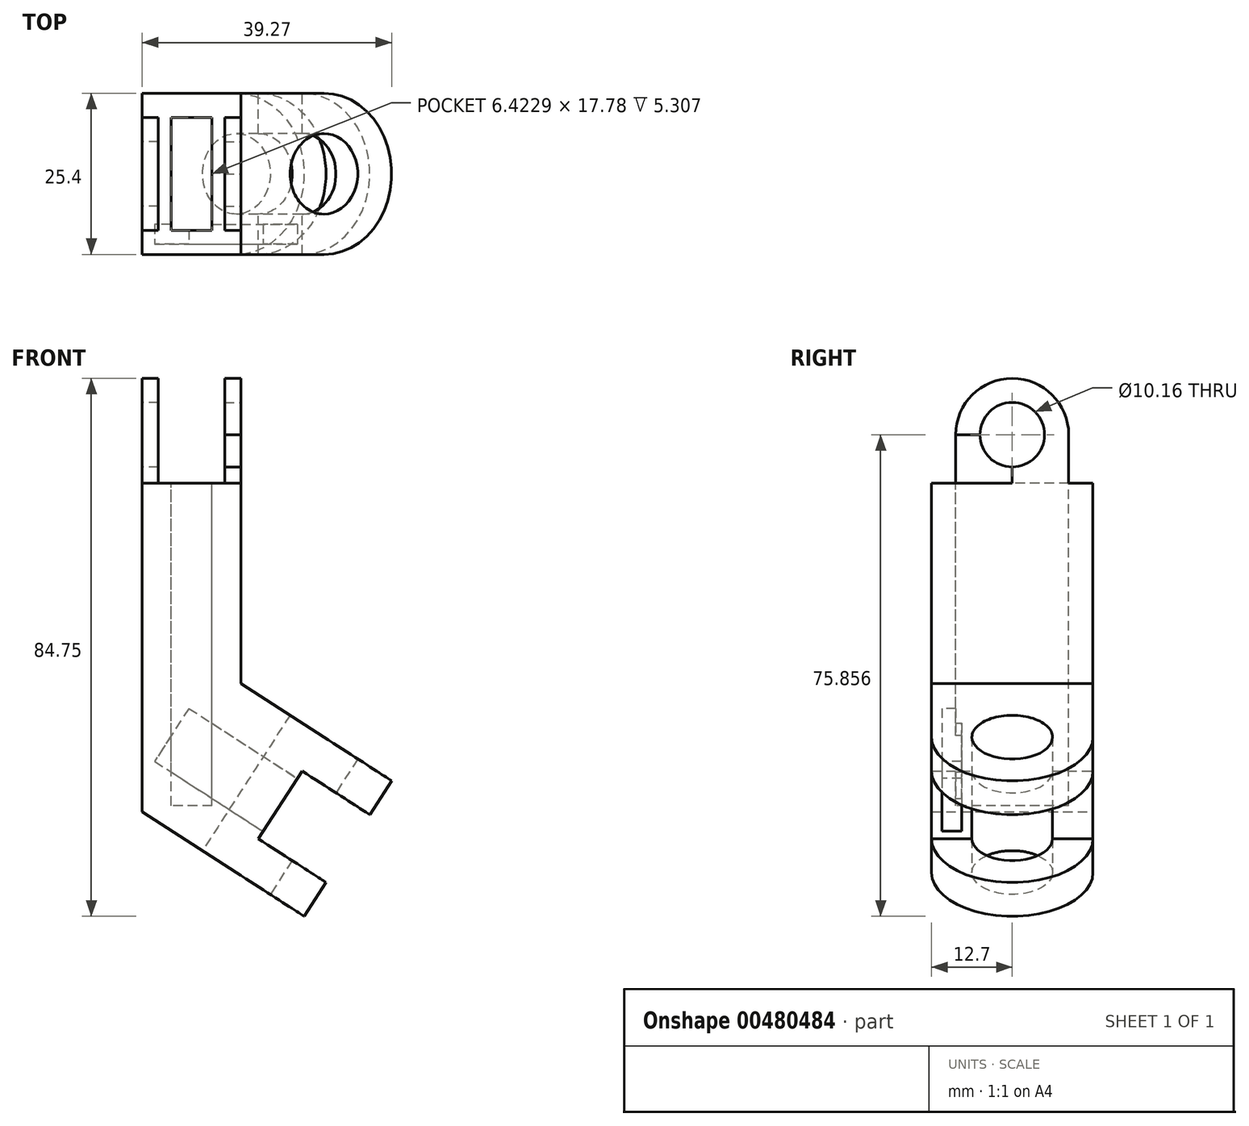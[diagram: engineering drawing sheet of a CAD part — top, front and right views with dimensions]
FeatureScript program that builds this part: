
annotation { "Feature Type Name" : "Feature", "Feature Type Description" : "" }
export const myFeature = defineFeature(function(context is Context, id is Id, definition is map)
    precondition{}
    {
        {
            var Q0;
            Q0=qCreatedBy(makeId("Front.planeOp"),FACE);
            var sketch = newSketch(context, id + "F0", { "sketchPlane" : qUnion([Q0])});
            skLineSegment(sketch, "E0", {"start": v(9.9, -37.3) * mm, "end": v(-3.19, -28.84) * mm});
            skLineSegment(sketch, "E1", {"start": v(-3.9, -58.63) * mm, "end": v(-18.71, -49.05) * mm});
            skLineSegment(sketch, "E2", {"start": v(-18.71, -49.05) * mm, "end": v(-18.71, 2.72) * mm});
            skLineSegment(sketch, "E3", {"start": v(-18.71, 2.72) * mm, "end": v(-3.19, 2.72) * mm});
            skLineSegment(sketch, "E4", {"start": v(-3.06, -57.34) * mm, "end": v(9.35, -38.14) * mm});
            skPoint(sketch, "E5.start.orphan", {"position": v(9.92, -52.43) * mm});
            skLineSegment(sketch, "E6", {"start": v(-3.06, -57.34) * mm, "end": v(-3.9, -58.63) * mm});
            skLineSegment(sketch, "E7", {"start": v(-3.9, -58.63) * mm, "end": v(9.9, -37.3) * mm});
            skPoint(sketch, "E8.orphan", {"position": v(3.03, -63.1) * mm});
            skPoint(sketch, "E9.start.orphan", {"position": v(5.9, -63.13) * mm});
            skPoint(sketch, "E10.start.orphan", {"position": v(18.01, -44.36) * mm});
            skPoint(sketch, "E11.orphan", {"position": v(16.81, -41.76) * mm});
            skLineSegment(sketch, "E12", {"start": v(-3.19, 2.72) * mm, "end": v(-3.19, -28.84) * mm});
            skPoint(sketch, "E13.orphan", {"position": v(-4.93, -27.71) * mm});
            skSolve(sketch);
        }
        {
            var Q0;
            {var subQ1=sQuery(id+"F0.wireOp",EDGE,"E0");Q0=makeQuery(id+"F0.imprint","IMPRINT",FACE,{"disambiguationData":[TD([[makeQuery(id+"F0.imprint","IMPRINT",EDGE,{"derivedFrom":subQ1}),1.0]])]});}
            extrude(context, id + "F1", {"entities" : qUnion([Q0]), "depth" : 25.4 * mm, "offsetDistance" : 25.4 * mm});
        }
        {
            var Q0;
            Q0=makeQuery(id+"F1.opExtrude","SWEPT_FACE",FACE,{"disambiguationData":[OSD([sQuery(id+"F0.wireOp",EDGE,"E12")])]});
            var sketch = newSketch(context, id + "F2", { "sketchPlane" : qUnion([Q0])});
            skLineSegment(sketch, "E14", {"start": v(-12.7, 2.72) * mm, "end": v(-12.7, 10.34) * mm});
            skCircle(sketch, "E15", {"center": v(-12.7, 10.34) * mm, "radius": 5.08 * mm});
            skLineSegment(sketch, "E16", {"start": v(-12.7, 10.34) * mm, "end": v(-3.81, 10.34) * mm});
            skArc(sketch, "E17", {"start": v(-3.81, 10.34) * mm, "mid": v(-12.7, 19.23) * mm, "end": v(-21.6, 10.34) * mm});
            skLineSegment(sketch, "E18", {"start": v(-12.7, 10.34) * mm, "end": v(-21.6, 10.34) * mm});
            skLineSegment(sketch, "E19", {"start": v(-21.6, 10.34) * mm, "end": v(-21.6, 2.72) * mm});
            skLineSegment(sketch, "E20", {"start": v(-21.6, 2.72) * mm, "end": v(-21.6, 10.34) * mm});
            skLineSegment(sketch, "E21", {"start": v(-3.81, 10.34) * mm, "end": v(-3.81, 2.72) * mm});
            skSolve(sketch);
        }
        {
            var Q0;
            {var subQ0=sQuery(id+"F2.wireOp",EDGE,"E20");Q0=makeQuery(id+"F2.imprint","IMPRINT",FACE,{"disambiguationData":[TD([[makeQuery(id+"F2.imprint","IMPRINT",EDGE,{"derivedFrom":subQ0}),-1.0]])]});}
            var Q1;
            {var subQ0=sQuery(id+"F2.wireOp",EDGE,"E21");Q1=makeQuery(id+"F2.imprint","IMPRINT",FACE,{"disambiguationData":[TD([[makeQuery(id+"F2.imprint","IMPRINT",EDGE,{"derivedFrom":subQ0}),-1.0]])]});}
            var Q2;
            {var subQ5=sQuery(id+"F2.wireOp",EDGE,"E17");Q2=makeQuery(id+"F2.imprint","IMPRINT",FACE,{"disambiguationData":[TD([[makeQuery(id+"F2.imprint","IMPRINT",EDGE,{"derivedFrom":subQ5}),1.0]])]});}
            extrude(context, id + "F3", {"entities" : qUnion([Q0, Q1, Q2]), "operationType" : NewBodyOperationType.ADD, "depth" : -2.54 * mm, "offsetDistance" : 25.4 * mm});
        }
        {
            var Q0;
            Q0=makeQuery(id+"F1.opExtrude","SWEPT_FACE",FACE,{"disambiguationData":[OSD([sQuery(id+"F0.wireOp",EDGE,"E2")])]});
            var sketch = newSketch(context, id + "F4", { "sketchPlane" : qUnion([Q0])});
            skLineSegment(sketch, "E22", {"start": v(12.7, 2.72) * mm, "end": v(12.7, 5.26) * mm});
            skCircle(sketch, "E23", {"center": v(12.7, 10.34) * mm, "radius": 5.08 * mm});
            skArc(sketch, "E24", {"start": v(21.6, 10.34) * mm, "mid": v(12.7, 19.23) * mm, "end": v(3.81, 10.34) * mm});
            skLineSegment(sketch, "E25", {"start": v(12.7, 10.34) * mm, "end": v(21.6, 10.34) * mm});
            skLineSegment(sketch, "E26", {"start": v(21.6, 10.34) * mm, "end": v(3.81, 10.34) * mm});
            skLineSegment(sketch, "E27", {"start": v(3.81, 10.34) * mm, "end": v(3.81, 2.72) * mm});
            skLineSegment(sketch, "E28", {"start": v(3.81, 2.72) * mm, "end": v(21.76, 2.72) * mm});
            skLineSegment(sketch, "E29", {"start": v(21.6, 10.34) * mm, "end": v(21.6, 2.72) * mm});
            skSolve(sketch);
        }
        {
            var Q0;
            Q0 = qSketchRegion(id + "F4", true);
            extrude(context, id + "F5", {"entities" : qUnion([Q0]), "operationType" : NewBodyOperationType.ADD, "depth" : -2.54 * mm, "offsetDistance" : 25.4 * mm});
        }
        {
            var Q0;
            Q0=makeQuery(id+"F1.opExtrude","SWEPT_FACE",FACE,{"disambiguationData":[OSD([sQuery(id+"F0.wireOp",EDGE,"E1")])]});
            var sketch = newSketch(context, id + "F6", { "sketchPlane" : qUnion([Q0])});
            skArc(sketch, "E30", {"start": v(28.55, 0) * mm, "mid": v(41.25, 12.7) * mm, "end": v(28.55, 25.4) * mm});
            skCircle(sketch, "E31", {"center": v(28.55, 12.7) * mm, "radius": 5.08 * mm});
            skLineSegment(sketch, "E32", {"start": v(28.55, 25.4) * mm, "end": v(28.55, 0) * mm});
            skSolve(sketch);
        }
        {
            var Q0;
            Q0=makeQuery(id+"F1.opExtrude","SWEPT_FACE",FACE,{"disambiguationData":[OSD([sQuery(id+"F0.wireOp",EDGE,"E0")])]});
            var sketch = newSketch(context, id + "F7", { "sketchPlane" : qUnion([Q0])});
            skArc(sketch, "E33", {"start": v(28.55, -25.4) * mm, "mid": v(41.25, -12.7) * mm, "end": v(28.55, 0) * mm});
            skCircle(sketch, "E34", {"center": v(28.55, -12.7) * mm, "radius": 5.08 * mm});
            skLineSegment(sketch, "E35", {"start": v(28.55, -25.4) * mm, "end": v(28.55, 0) * mm});
            skSolve(sketch);
        }
        {
            var Q0;
            {var subQ0=sQuery(id+"F7.wireOp",EDGE,"E33");Q0=makeQuery(id+"F7.imprint","IMPRINT",FACE,{"disambiguationData":[TD([[makeQuery(id+"F7.imprint","IMPRINT",EDGE,{"derivedFrom":subQ0}),1.0]])]});}
            extrude(context, id + "F8", {"entities" : qUnion([Q0]), "operationType" : NewBodyOperationType.ADD, "depth" : -6.35 * mm, "offsetDistance" : 25.4 * mm});
        }
        {
            var Q0;
            {var subQ0=sQuery(id+"F6.wireOp",EDGE,"E30");Q0=makeQuery(id+"F6.imprint","IMPRINT",FACE,{"disambiguationData":[TD([[makeQuery(id+"F6.imprint","IMPRINT",EDGE,{"derivedFrom":subQ0}),1.0]])]});}
            extrude(context, id + "F9", {"entities" : qUnion([Q0]), "operationType" : NewBodyOperationType.ADD, "depth" : -6.35 * mm, "offsetDistance" : 25.4 * mm});
        }
        {
            var Q0;
            Q0=sQuery(id+"F6.wireOp",VERTEX,"E31.center");
            var Q1;
            Q1=makeQuery(id+"F1.opExtrude","SWEPT_BODY",BODY,{"disambiguationData":[OSD([sQuery(id+"F0.wireOp",EDGE,"E0"),sQuery(id+"F0.wireOp",EDGE,"E1"),sQuery(id+"F0.wireOp",EDGE,"E2"),sQuery(id+"F0.wireOp",EDGE,"E3"),sQuery(id+"F0.wireOp",EDGE,"E7"),sQuery(id+"F0.wireOp",EDGE,"E12")])]});
            hole(context, id + "F10", {"style" : HoleStyle.SIMPLE, "endStyle" : HoleEndStyle.BLIND, "holeDiameter" : 12.7 * mm, "majorDiameter" : 6.35 * mm, "holeDepth" : 50.8 * mm, "isTappedThrough" : true, "tappedDepth" : 12.7 * mm, "tapClearance" : 3, "locations" : qUnion([Q0]), "scope" : qUnion([Q1])});
        }
        {
            var Q0;
            {var subQ3=sQuery(id+"F0.wireOp",EDGE,"E7");Q0=makeQuery(id+"F10.hole-0.boolean.opBoolean","SPLIT",FACE,{"disambiguationData":[TD([makeQuery(id+"F1.opExtrude","CAP_FACE",FACE,{"disambiguationData":[OSD([sQuery(id+"F0.wireOp",EDGE,"E0"),sQuery(id+"F0.wireOp",EDGE,"E1"),sQuery(id+"F0.wireOp",EDGE,"E2"),sQuery(id+"F0.wireOp",EDGE,"E3"),subQ3,sQuery(id+"F0.wireOp",EDGE,"E12")])],"isStart":false})])],"derivedFrom":makeQuery(id+"F1.opExtrude","SWEPT_FACE",FACE,{"disambiguationData":[OSD([subQ3])]})});}
            var sketch = newSketch(context, id + "F11", { "sketchPlane" : qUnion([Q0])});
            skLineSegment(sketch, "E36", {"start": v(-17.78, -32.3) * mm, "end": v(-17.78, -45) * mm});
            skLineSegment(sketch, "E37", {"start": v(-19.05, -45) * mm, "end": v(-25.4, -45) * mm});
            skLineSegment(sketch, "E38.bottom", {"start": v(-20.66, -33.69) * mm, "end": v(-23.8, -33.69) * mm});
            skLineSegment(sketch, "E38.top", {"start": v(-20.66, -43.61) * mm, "end": v(-23.8, -43.61) * mm});
            skLineSegment(sketch, "E38.left", {"start": v(-20.66, -33.69) * mm, "end": v(-20.66, -43.61) * mm});
            skLineSegment(sketch, "E38.right", {"start": v(-23.8, -33.69) * mm, "end": v(-23.8, -43.61) * mm});
            skPoint(sketch, "E38.middle", {"position": v(-22.23, -38.65) * mm});
            skPoint(sketch, "E39.orphan", {"position": v(-25.4, -32.3) * mm});
            skSolve(sketch);
        }
        {
            var Q0;
            Q0=makeQuery(id+"F1.opExtrude","SWEPT_FACE",FACE,{"disambiguationData":[OSD([sQuery(id+"F0.wireOp",EDGE,"E3")])]});
            var sketch = newSketch(context, id + "F12", { "sketchPlane" : qUnion([Q0])});
            skLineSegment(sketch, "E40", {"start": v(-14.16, -7.45) * mm, "end": v(-7.74, -17.95) * mm});
            skLineSegment(sketch, "E41", {"start": v(-3.19, -25.4) * mm, "end": v(-3.19, 0) * mm});
            skLineSegment(sketch, "E42", {"start": v(-7.74, -7.45) * mm, "end": v(-14.16, -17.95) * mm});
            skLineSegment(sketch, "E43.bottom", {"start": v(-7.74, -3.81) * mm, "end": v(-14.16, -3.81) * mm});
            skLineSegment(sketch, "E43.top", {"start": v(-7.74, -21.59) * mm, "end": v(-14.16, -21.59) * mm});
            skLineSegment(sketch, "E43.left", {"start": v(-7.74, -3.81) * mm, "end": v(-7.74, -21.59) * mm});
            skLineSegment(sketch, "E43.right", {"start": v(-14.16, -3.81) * mm, "end": v(-14.16, -21.59) * mm});
            skPoint(sketch, "E43.middle", {"position": v(-10.95, -12.7) * mm});
            skPoint(sketch, "E44.orphan", {"position": v(-18.71, 0) * mm});
            skSolve(sketch);
        }
        {
            var Q0;
            {var subQ0=sQuery(id+"F12.wireOp",EDGE,"E43.top");Q0=makeQuery(id+"F12.imprint","IMPRINT",FACE,{"disambiguationData":[TD([[makeQuery(id+"F12.imprint","IMPRINT",EDGE,{"derivedFrom":subQ0}),-1.0]])]});}
            var Q1;
            {var subQ0=sQuery(id+"F12.wireOp",EDGE,"E43.right");var subQ1=sQuery(id+"F12.wireOp",EDGE,"E40");var subQ2=makeQuery(id+"F12.imprint","INTERSECT",VERTEX,{"derivedFrom":[subQ1,subQ0]});Q1=makeQuery(id+"F12.imprint","IMPRINT",FACE,{"disambiguationData":[TD([[makeQuery(id+"F12.imprint","IMPRINT",EDGE,{"disambiguationData":[TD([[subQ2,-1.0]])],"derivedFrom":subQ1}),-1.0]])]});}
            var Q2;
            {var subQ0=sQuery(id+"F12.wireOp",EDGE,"E43.left");var subQ1=sQuery(id+"F12.wireOp",EDGE,"E40");var subQ2=makeQuery(id+"F12.imprint","INTERSECT",VERTEX,{"derivedFrom":[subQ1,subQ0]});Q2=makeQuery(id+"F12.imprint","IMPRINT",FACE,{"disambiguationData":[TD([[makeQuery(id+"F12.imprint","IMPRINT",EDGE,{"disambiguationData":[TD([[subQ2,1.0]])],"derivedFrom":subQ1}),1.0]])]});}
            var Q3;
            {var subQ3=sQuery(id+"F12.wireOp",EDGE,"E43.bottom");Q3=makeQuery(id+"F12.imprint","IMPRINT",FACE,{"disambiguationData":[TD([[makeQuery(id+"F12.imprint","IMPRINT",EDGE,{"derivedFrom":subQ3}),1.0]])]});}
            extrude(context, id + "F13", {"entities" : qUnion([Q0, Q1, Q2, Q3]), "operationType" : NewBodyOperationType.REMOVE, "oppositeDirection" : true, "depth" : 50.8 * mm, "offsetDistance" : 25.4 * mm});
        }
        {
            var Q0;
            Q0=makeQuery(id+"F11.imprint","IMPRINT",FACE,{"disambiguationData":[TD([[makeQuery(id+"F11.imprint","IMPRINT",EDGE,{"derivedFrom":sQuery(id+"F11.wireOp",EDGE,"E38.bottom")}),1.0]])]});
            extrude(context, id + "F14", {"entities" : qUnion([Q0]), "operationType" : NewBodyOperationType.REMOVE, "oppositeDirection" : true, "depth" : 20.32 * mm, "offsetDistance" : 25.4 * mm});
        }
    });
